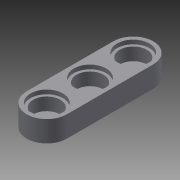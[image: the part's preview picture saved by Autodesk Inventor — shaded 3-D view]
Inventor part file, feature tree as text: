
AUTODESK INVENTOR PART (.ipt)
format: ipt  version: 2013 (Build 170138000, 138)  size: 126,464 bytes
history: native  units: mm
features: extrude x4, sketch x1, pattern_linear x1, plane x1
ambient origin geometry x8: Origin, YZ Plane, XZ Plane, XY Plane, X Axis, Y Axis, Z Axis, Center Point
bodies: Solid1 (feature_tree)
feature tree (7):
  sketch  "Sketch1"  dims[d1=5.0mm d2=6.0mm d3=3.7mm d4=0.0mm d5=3.9mm d6=0.0mm d7=3.9mm d8=0.0mm d9=2.4mm d10=0.0mm d11=10.0mm d13=8.0mm d14=-0.05mm d15=2.4mm d16=0.0mm d17=16.0mm d18=30.0mm d20=-8.0mm]
  extrude  "Extrusion1"  Depth=6.0mm
  extrude  "Extrusion2"  Depth=3.7mm
  extrude  "Extrusion3"  TaperAngle=0.0deg  [1 undecoded]
  pattern_linear  "Rectangular Pattern1"  Spacing1=3.9mm  [1 undecoded]
  plane  "Work Plane1"
  extrude  "Extrusion4"  Depth=3.9mm TaperAngle=0.0deg
note: 2 required parameter values undecoded (feature->parameter linkage not recoverable at this tier; creation-order binding heuristic only, values carry confidence <= 0.55)
